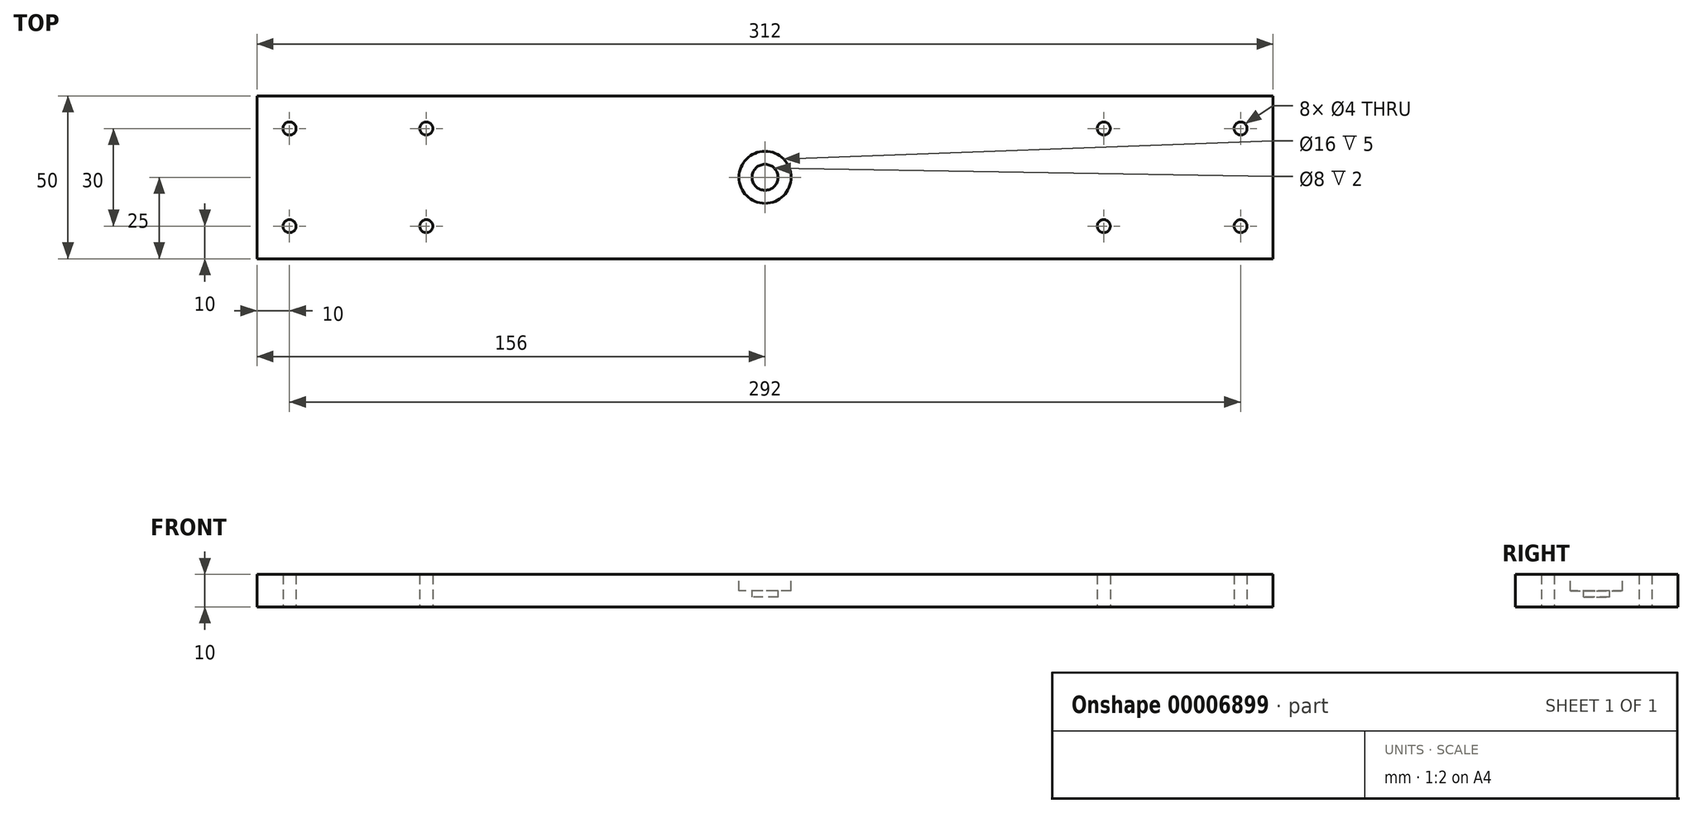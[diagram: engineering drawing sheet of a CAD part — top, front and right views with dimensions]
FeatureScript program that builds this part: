
annotation { "Feature Type Name" : "Feature", "Feature Type Description" : "" }
export const myFeature = defineFeature(function(context is Context, id is Id, definition is map)
    precondition{}
    {
        {
            var Q0;
            Q0=qCreatedBy(makeId("Top.planeOp"),FACE);
            var sketch = newSketch(context, id + "F0", { "sketchPlane" : qUnion([Q0])});
            skLineSegment(sketch, "E0.rect.bottom", {"start": v(156, -25) * mm, "end": v(-156, -25) * mm});
            skLineSegment(sketch, "E0.rect.top", {"start": v(156, 25) * mm, "end": v(-156, 25) * mm});
            skLineSegment(sketch, "E0.rect.left", {"start": v(156, -25) * mm, "end": v(156, 25) * mm});
            skLineSegment(sketch, "E0.rect.right", {"start": v(-156, -25) * mm, "end": v(-156, 25) * mm});
            skPoint(sketch, "E0.rect.middle", {"position": v(0, 0) * mm});
            skCircle(sketch, "E1", {"center": v(-146, 15) * mm, "radius": 2 * mm});
            skCircle(sketch, "E2", {"center": v(-104, 15) * mm, "radius": 2 * mm});
            skCircle(sketch, "E3", {"center": v(-146, -15) * mm, "radius": 2 * mm});
            skCircle(sketch, "E4", {"center": v(-104, -15) * mm, "radius": 2 * mm});
            skCircle(sketch, "E5", {"center": v(146, -15) * mm, "radius": 2 * mm});
            skCircle(sketch, "E6", {"center": v(104, -15) * mm, "radius": 2 * mm});
            skCircle(sketch, "E7", {"center": v(146, 15) * mm, "radius": 2 * mm});
            skCircle(sketch, "E8", {"center": v(104, 15) * mm, "radius": 2 * mm});
            skLineSegment(sketch, "E9", {"start": v(-113, 0) * mm, "end": v(185, 0) * mm, "construction": true});
            skLineSegment(sketch, "E10", {"start": v(0, 88.94) * mm, "end": v(0, -137.61) * mm, "construction": true});
            skSolve(sketch);
        }
        {
            var Q0;
            Q0=qSketchRegion(id+"F0",true);
            var Q1;
            Q1=makeQuery(id+"F0.imprint","IMPRINT",FACE,{"disambiguationData":[TD([[makeQuery(id+"F0.imprint","IMPRINT",EDGE,{"derivedFrom":sQuery(id+"F0.wireOp",EDGE,"E0.rect.bottom")}),-1.0]])]});
            extrude(context, id + "F1", {"entities" : qUnion([Q0, Q1]), "depth" : 10 * mm});
        }
        {
            var Q0;
            Q0=makeQuery(id+"F1.opExtrude","CAP_FACE",FACE,{"disambiguationData":[OSD([sQuery(id+"F0.wireOp",EDGE,"E0.rect.bottom"),sQuery(id+"F0.wireOp",EDGE,"E0.rect.top"),sQuery(id+"F0.wireOp",EDGE,"E0.rect.left"),sQuery(id+"F0.wireOp",EDGE,"E0.rect.right"),sQuery(id+"F0.wireOp",EDGE,"E1"),sQuery(id+"F0.wireOp",EDGE,"E2"),sQuery(id+"F0.wireOp",EDGE,"E3"),sQuery(id+"F0.wireOp",EDGE,"E4"),sQuery(id+"F0.wireOp",EDGE,"E5"),sQuery(id+"F0.wireOp",EDGE,"E6"),sQuery(id+"F0.wireOp",EDGE,"E7"),sQuery(id+"F0.wireOp",EDGE,"E8")])],"isStart":false});
            var sketch = newSketch(context, id + "F2", { "sketchPlane" : qUnion([Q0])});
            skCircle(sketch, "E11", {"center": v(0, 0) * mm, "radius": 8 * mm});
            skSolve(sketch);
        }
        {
            var Q0;
            Q0=qSketchRegion(id+"F2",true);
            extrude(context, id + "F3", {"entities" : qUnion([Q0]), "operationType" : NewBodyOperationType.REMOVE, "oppositeDirection" : true, "depth" : (5) * mm});
        }
        {
            var Q0;
            Q0=makeQuery(id+"F3.boolean.opBoolean","COPY",FACE,{"derivedFrom":makeQuery(id+"F3.opExtrude","CAP_FACE",FACE,{"disambiguationData":[OSD([sQuery(id+"F2.wireOp",EDGE,"E11")])],"isStart":false})});
            var sketch = newSketch(context, id + "F4", { "sketchPlane" : qUnion([Q0])});
            skCircle(sketch, "E12", {"center": v(0, 0) * mm, "radius": 4 * mm});
            skSolve(sketch);
        }
        {
            var Q0;
            Q0=qSketchRegion(id+"F4",true);
            extrude(context, id + "F5", {"entities" : qUnion([Q0]), "operationType" : NewBodyOperationType.REMOVE, "oppositeDirection" : true, "depth" : (2) * mm});
        }
    });
